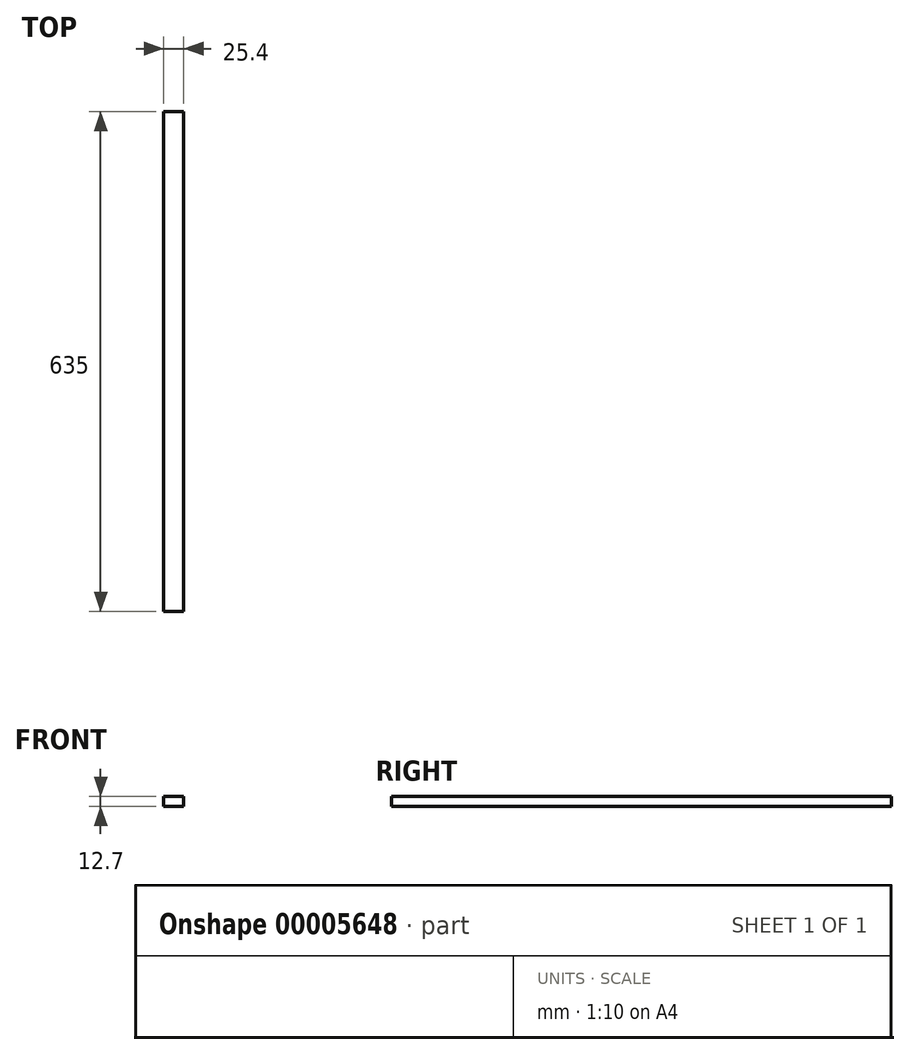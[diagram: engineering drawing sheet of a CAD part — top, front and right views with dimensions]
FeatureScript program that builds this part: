
annotation { "Feature Type Name" : "Feature", "Feature Type Description" : "" }
export const myFeature = defineFeature(function(context is Context, id is Id, definition is map)
    precondition{}
    {
        {
            var Q0;
            Q0=qCreatedBy(makeId("Top.planeOp"),FACE);
            var sketch = newSketch(context, id + "F0", { "sketchPlane" : qUnion([Q0])});
            skLineSegment(sketch, "E0.bottom", {"start": v(0, 0) * mm, "end": v(25.4, 0) * mm});
            skLineSegment(sketch, "E0.top", {"start": v(0, 635) * mm, "end": v(25.4, 635) * mm});
            skLineSegment(sketch, "E0.left", {"start": v(0, 0) * mm, "end": v(0, 635) * mm});
            skLineSegment(sketch, "E0.right", {"start": v(25.4, 0) * mm, "end": v(25.4, 635) * mm});
            skSolve(sketch);
        }
        {
            var Q0;
            Q0 = qSketchRegion(id + "F0", true);
            extrude(context, id + "F1", {"entities" : qUnion([Q0]), "depth" : 12.7 * mm});
        }
    });
